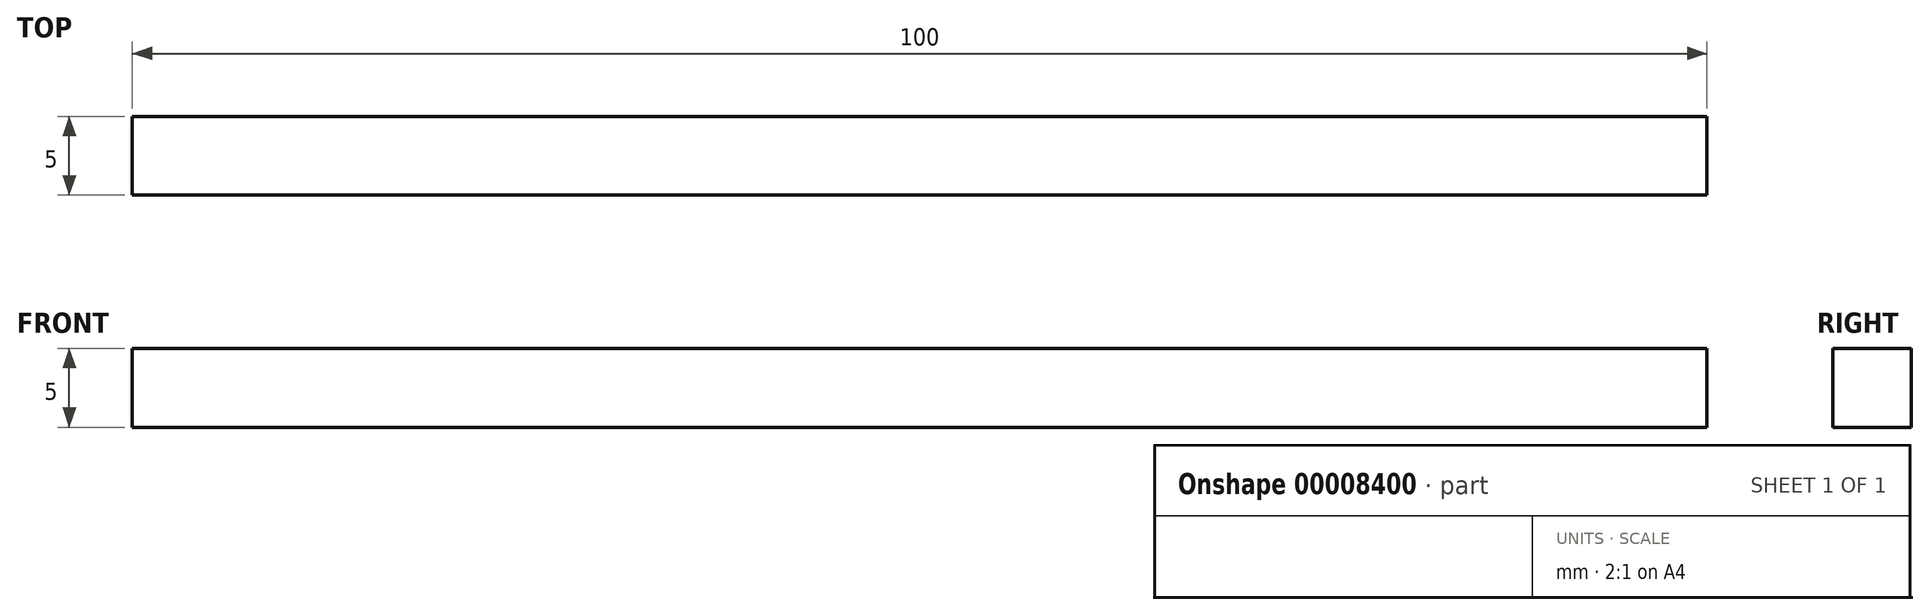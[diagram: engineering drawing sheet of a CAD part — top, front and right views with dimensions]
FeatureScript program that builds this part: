
annotation { "Feature Type Name" : "Feature", "Feature Type Description" : "" }
export const myFeature = defineFeature(function(context is Context, id is Id, definition is map)
    precondition{}
    {
        {
            var Q0;
            Q0=qCreatedBy(makeId("Top.planeOp"),FACE);
            var sketch = newSketch(context, id + "F0", { "sketchPlane" : qUnion([Q0])});
            skLineSegment(sketch, "E0.rect.bottom", {"start": v(-50, 2.5) * mm, "end": v(50, 2.5) * mm});
            skLineSegment(sketch, "E0.rect.top", {"start": v(-50, -2.5) * mm, "end": v(50, -2.5) * mm});
            skLineSegment(sketch, "E0.rect.left", {"start": v(-50, 2.5) * mm, "end": v(-50, -2.5) * mm});
            skLineSegment(sketch, "E0.rect.right", {"start": v(50, 2.5) * mm, "end": v(50, -2.5) * mm});
            skPoint(sketch, "E0.rect.middle", {"position": v(0, 0) * mm});
            skSolve(sketch);
        }
        {
            var Q0;
            Q0 = qSketchRegion(id + "F0", true);
            extrude(context, id + "F1", {"entities" : qUnion([Q0]), "depth" : 5 * mm});
        }
    });
